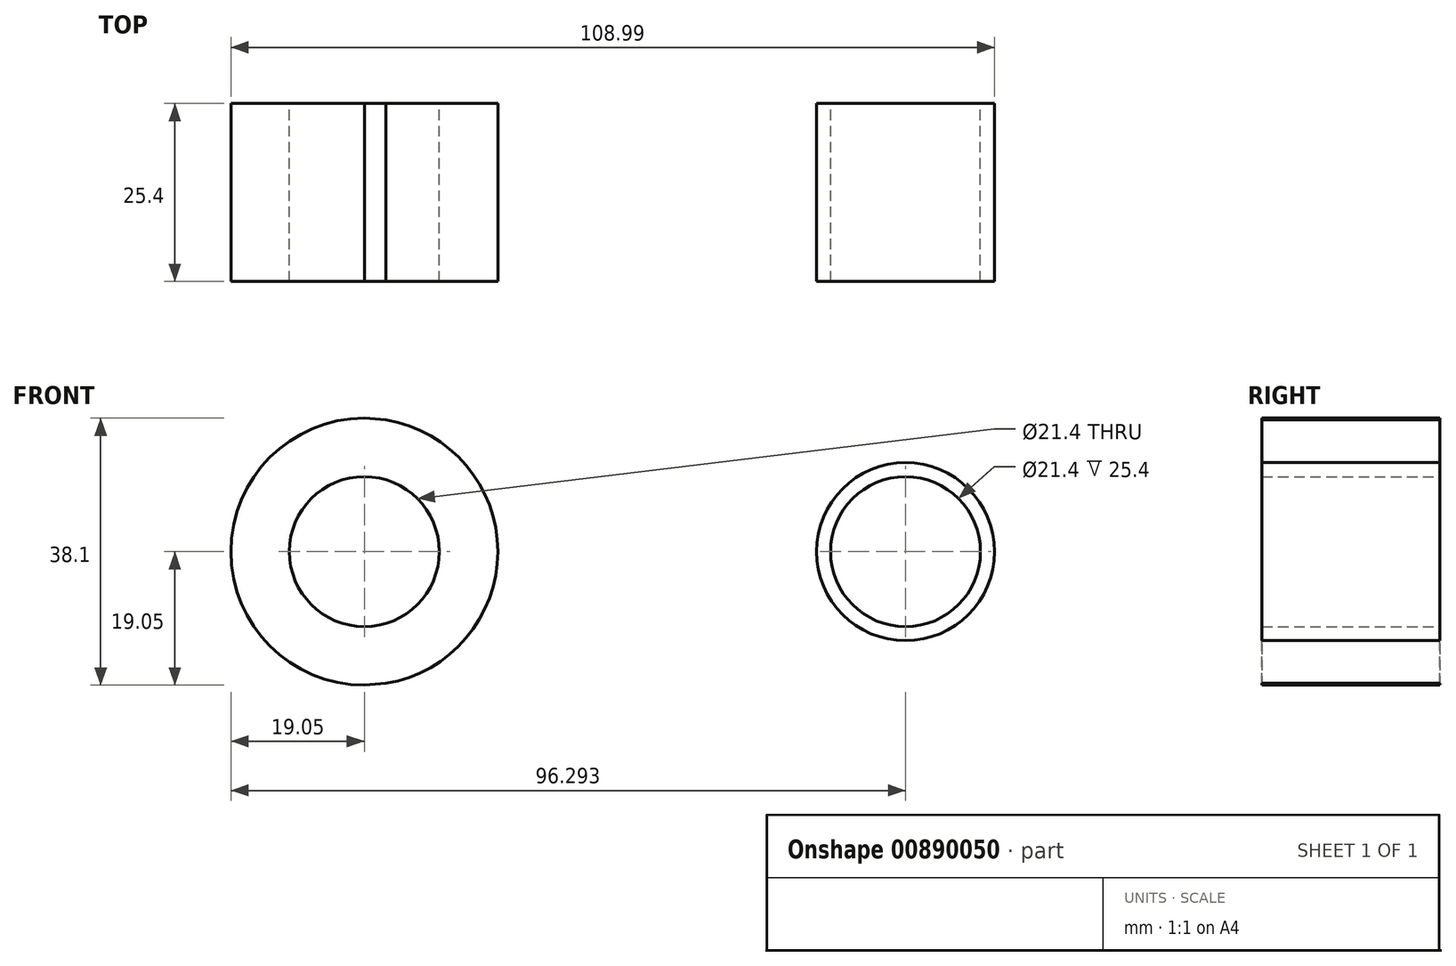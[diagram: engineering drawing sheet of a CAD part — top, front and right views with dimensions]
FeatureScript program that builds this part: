
annotation { "Feature Type Name" : "Feature", "Feature Type Description" : "" }
export const myFeature = defineFeature(function(context is Context, id is Id, definition is map)
    precondition{}
    {
        {
            var Q0;
            Q0=qCreatedBy(makeId("Front.planeOp"),FACE);
            var sketch = newSketch(context, id + "F0", { "sketchPlane" : qUnion([Q0])});
            skCircle(sketch, "E0", {"center": v(0, 0) * mm, "radius": 19.05 * mm});
            skCircle(sketch, "E1", {"center": v(77.24, 0) * mm, "radius": 12.7 * mm});
            skLineSegment(sketch, "E2", {"start": v(0, 19.05) * mm, "end": v(78.28, 12.66) * mm});
            skLineSegment(sketch, "E3", {"start": v(0, -19.05) * mm, "end": v(78.28, -12.66) * mm});
            skCircle(sketch, "E4", {"center": v(0, 0) * mm, "radius": 10.7 * mm});
            skCircle(sketch, "E5", {"center": v(77.24, 0) * mm, "radius": 10.7 * mm});
            skSolve(sketch);
        }
        {
            var Q0;
            Q0=makeQuery(id+"F0.imprint","IMPRINT",FACE,{"disambiguationData":[TD([[makeQuery(id+"F0.imprint","IMPRINT",EDGE,{"derivedFrom":sQuery(id+"F0.wireOp",EDGE,"E5")}),-1.0]])]});
            var Q1;
            {var subQ0=sQuery(id+"F0.wireOp",EDGE,"E2");var subQ1=sQuery(id+"F0.wireOp",EDGE,"E0");var subQ2=makeQuery(id+"F0.imprint","INTERSECT",VERTEX,{"disambiguationData":[OD(1.0)],"derivedFrom":[subQ1,subQ0]});Q1=makeQuery(id+"F0.imprint","IMPRINT",FACE,{"disambiguationData":[TD([[makeQuery(id+"F0.imprint","IMPRINT",EDGE,{"disambiguationData":[TD([[subQ2,1.0]])],"derivedFrom":subQ1}),-1.0]])]});}
            var Q2;
            Q2=makeQuery(id+"F0.imprint","IMPRINT",FACE,{"disambiguationData":[TD([[makeQuery(id+"F0.imprint","IMPRINT",EDGE,{"derivedFrom":sQuery(id+"F0.wireOp",EDGE,"E4")}),-1.0]])]});
            extrude(context, id + "F1", {"entities" : qUnion([Q0, Q1, Q2]), "depth" : 25.4 * mm, "offsetDistance" : 25.4 * mm});
        }
    });
